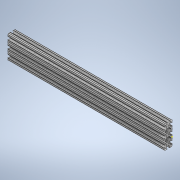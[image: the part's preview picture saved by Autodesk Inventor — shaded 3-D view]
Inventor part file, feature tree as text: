
AUTODESK INVENTOR PART (.ipt)
format: ipt  version: 2020 (Build 240168000, 168)  size: 375,808 bytes
history: native  units: in
note: dims shown in document units (in); Inventor stores cm internally (conversion verified against a paired STEP export)
features: sketch x2, extrude x1
ambient origin geometry x8: Origin, YZ Plane, XZ Plane, XY Plane, X Axis, Y Axis, Z Axis, Center Point
bodies: Solid1 (feature_tree)
feature tree (3):
  extrude  "Extrusion1"  [1 undecoded]
  sketch  "Sketch2"
  sketch  "Sketch1"  dims[d0=20.0in d1=0.0in]
note: 1 required parameter value undecoded (feature->parameter linkage not recoverable at this tier; creation-order binding heuristic only, values carry confidence <= 0.55)
